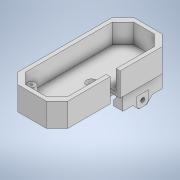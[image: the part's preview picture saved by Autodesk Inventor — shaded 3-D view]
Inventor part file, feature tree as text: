
AUTODESK INVENTOR PART (.ipt)
format: ipt  version: 2020 (Build 240168000, 168)  size: 300,544 bytes
history: native  units: mm
features: sketch x14, extrude x13, projected_geometry x4, chamfer x1, fillet x1
ambient origin geometry x8: Origin, YZ Plane, XZ Plane, XY Plane, X Axis, Y Axis, Z Axis, Center Point
bodies: Volumenkörper1 (feature_tree)
feature tree (33):
  extrude  "Extrusion1"  Depth=55.0mm
  extrude  "Extrusion2"  Depth=5.5mm
  extrude  "Extrusion3"  Depth=5.5mm
  extrude  "Extrusion5"  Depth=5.5mm
  extrude  "Extrusion6"  Depth=5.5mm
  extrude  "Extrusion7"  Depth=2.0mm
  extrude  "Extrusion8"  Depth=5.5mm
  extrude  "Extrusion9"  Depth=5.5mm
  extrude  "Extrusion10"  Depth=5.5mm
  extrude  "Extrusion11"  Depth=5.5mm
  extrude  "Extrusion12"  Depth=2.0mm TaperAngle=0.0deg
  chamfer  "Fase1"  Distance=18.3mm
  fillet  "Rundung1"  Radius=4.0mm
  sketch  "Skizze14"  dims[d24=2.0mm]
  extrude  "Extrusion13"  Depth=0.001mm
  extrude  "Extrusion14"  Depth=0.001mm
  sketch  "Skizze1"  dims[d0=21.5mm d1=55.0mm]
  sketch  "Skizze3"  dims[d2=5.5mm d3=5.5mm]
  projected_geometry  "Projizierte Kontur1"
  sketch  "Skizze4"  dims[d4=5.5mm d5=5.5mm]
  sketch  "Skizze6"  dims[d6=5.5mm d7=5.5mm]
  sketch  "Skizze7"  dims[d8=5.5mm d9=5.5mm]
  sketch  "Skizze8"  dims[d10=2.0mm d11=2.0mm]
  sketch  "Skizze9"  dims[d12=5.5mm d13=5.5mm]
  sketch  "Skizze10"  dims[d14=5.5mm d15=5.5mm]
  sketch  "Skizze11"  dims[d16=5.5mm d17=5.5mm]
  sketch  "Skizze12"  dims[d18=5.5mm d19=5.5mm]
  projected_geometry  "Projizierte Kontur2"
  sketch  "Skizze13"  dims[d20=10.0mm d21=0.0mm d22=2.0mm d23=0.0mm]
  sketch  "Skizze15"  dims[d25=21.0mm]
  projected_geometry  "Projizierte Kontur3"
  sketch  "Skizze16"  dims[d26=2.0mm d27=18.3mm d28=4.0mm d29=4.0mm d30=1.1mm d31=1.1mm d32=5.0mm d33=0.0mm d38=20.0mm d39=12.0mm d40=0.0mm d41=8.2mm d42=0.0mm d43=0.0mm d44=5.0mm d45=12.0mm d46=0.0mm d47=12.0mm d48=0.0mm d49=5.0mm d50=0.0mm d51=0.0mm d52=10.0mm d53=6.0mm d54=6.0mm d55=0.001mm d56=4.0mm d57=0.0mm d58=0.0mm d59=4.0mm d60=4.0mm d61=0.0mm d62=0.0mm d63=2.1mm d64=0.0mm d65=0.0mm d66=2.0mm d67=2.0mm d68=45.0deg d69=2.0mm d70=0.001mm d71=0.0mm d72=0.001mm d73=0.0mm]
  projected_geometry  "Projizierte Kontur4"
